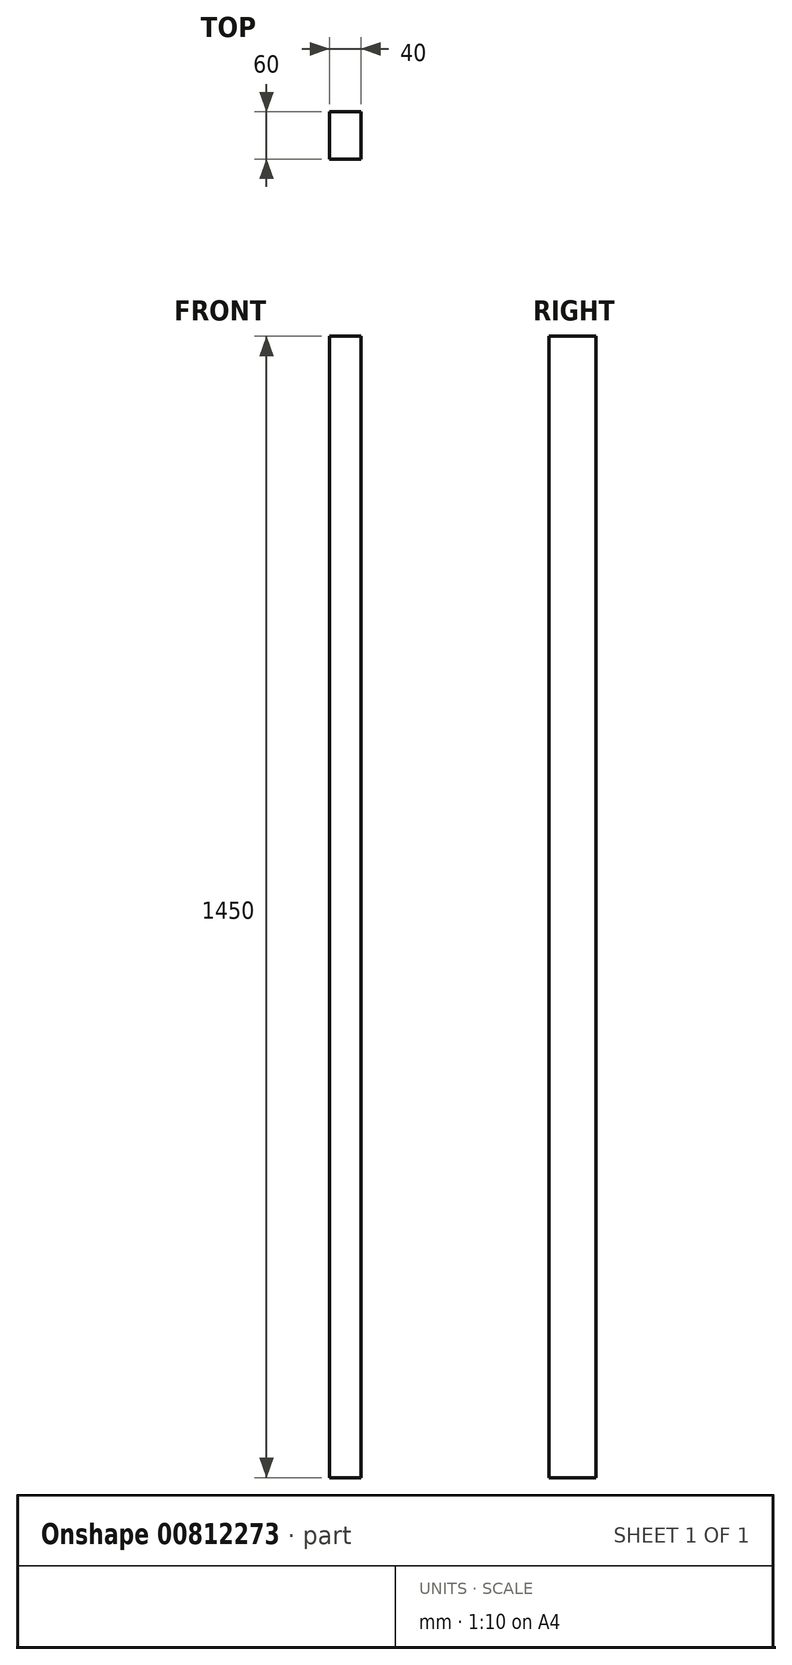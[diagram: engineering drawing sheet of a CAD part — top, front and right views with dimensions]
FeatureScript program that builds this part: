
annotation { "Feature Type Name" : "Feature", "Feature Type Description" : "" }
export const myFeature = defineFeature(function(context is Context, id is Id, definition is map)
    precondition{}
    {
        {
            var Q0;
            Q0=qCreatedBy(makeId("Front.planeOp"),FACE);
            var sketch = newSketch(context, id + "F0", { "sketchPlane" : qUnion([Q0])});
            skLineSegment(sketch, "E0.bottom", {"start": v(20, -725) * mm, "end": v(-20, -725) * mm});
            skLineSegment(sketch, "E0.top", {"start": v(20, 725) * mm, "end": v(-20, 725) * mm});
            skLineSegment(sketch, "E0.left", {"start": v(20, -725) * mm, "end": v(20, 725) * mm});
            skLineSegment(sketch, "E0.right", {"start": v(-20, -725) * mm, "end": v(-20, 725) * mm});
            skPoint(sketch, "E0.middle", {"position": v(0, 0) * mm});
            skSolve(sketch);
        }
        {
            var Q0;
            Q0=makeQuery(id+"F0.imprint","IMPRINT",FACE,{"disambiguationData":[TD([[makeQuery(id+"F0.imprint","IMPRINT",EDGE,{"derivedFrom":sQuery(id+"F0.wireOp",EDGE,"E0.bottom")}),-1.0]])]});
            var Q1;
            Q1=sQuery(id+"F0.wireOp",EDGE,"E0.right");
            extrude(context, id + "F1", {"entities" : qUnion([Q0]), "surfaceEntities" : qUnion([Q1]), "depth" : 60 * mm, "offsetDistance" : 25 * mm});
        }
    });
